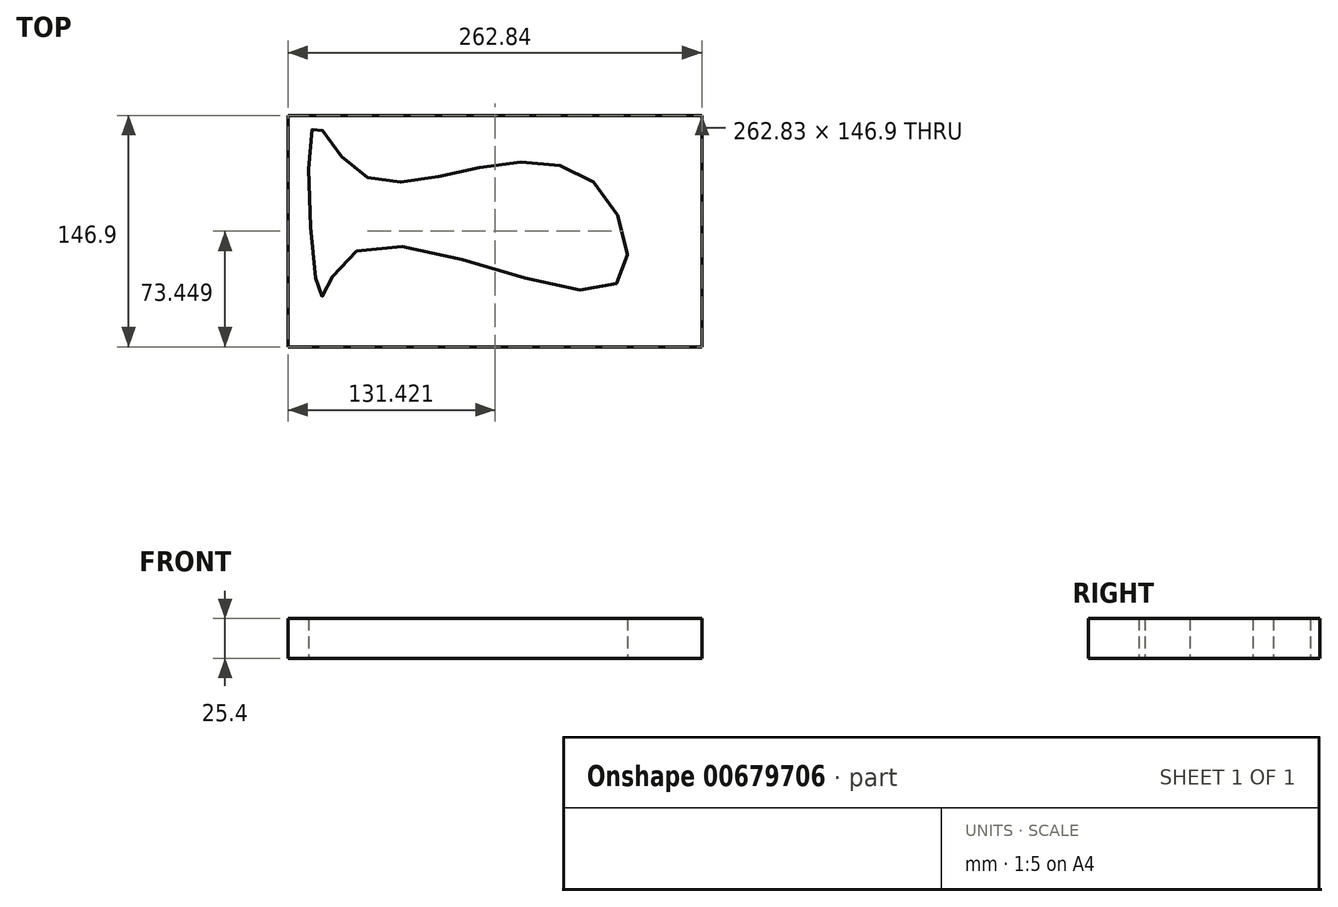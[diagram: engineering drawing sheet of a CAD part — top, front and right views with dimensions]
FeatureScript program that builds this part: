
annotation { "Feature Type Name" : "Feature", "Feature Type Description" : "" }
export const myFeature = defineFeature(function(context is Context, id is Id, definition is map)
    precondition{}
    {
        {
            var Q0;
            Q0=qCreatedBy(makeId("Top.planeOp"),FACE);
            var sketch = newSketch(context, id + "F0", { "sketchPlane" : qUnion([Q0])});
            skLineSegment(sketch, "E0.bottom", {"start": v(-124.76, 81) * mm, "end": v(138.08, 81) * mm});
            skLineSegment(sketch, "E0.top", {"start": v(-124.76, -65.89) * mm, "end": v(138.08, -65.89) * mm});
            skLineSegment(sketch, "E0.left", {"start": v(-124.76, 81) * mm, "end": v(-124.76, -65.89) * mm});
            skLineSegment(sketch, "E0.right", {"start": v(138.08, 81) * mm, "end": v(138.08, -65.89) * mm});
            skSolve(sketch);
        }
        {
            var Q0;
            Q0 = qSketchRegion(id + "F0", true);
            extrude(context, id + "F1", {"entities" : qUnion([Q0]), "depth" : 25.4 * mm, "offsetDistance" : 25.4 * mm});
        }
        {
            var Q0;
            Q0=makeQuery(id+"F1.opExtrude","CAP_FACE",FACE,{"disambiguationData":[OSD([sQuery(id+"F0.wireOp",EDGE,"E0.bottom"),sQuery(id+"F0.wireOp",EDGE,"E0.top"),sQuery(id+"F0.wireOp",EDGE,"E0.left"),sQuery(id+"F0.wireOp",EDGE,"E0.right")])],"isStart":false});
            var sketch = newSketch(context, id + "F2", { "sketchPlane" : qUnion([Q0])});
            skFitSpline(sketch, "E1", {"points": [v(-81.26, -4.94) * mm, v(80.86, -27.62) * mm, v(71.9, 36.22) * mm, v(-10.98, 46.3) * mm, v(-83.22, 46.86) * mm, v(-108.7, 74.02) * mm, v(-104.23, -33.5) * mm, v(-81.26, -4.94) * mm]});
            skSolve(sketch);
        }
        {
            var Q0;
            Q0=makeQuery(id+"F2.imprint","IMPRINT",FACE,{"disambiguationData":[TD([[makeQuery(id+"F2.imprint","IMPRINT",EDGE,{"derivedFrom":sQuery(id+"F2.wireOp",EDGE,"E1")}),1.0]])]});
            extrude(context, id + "F3", {"entities" : qUnion([Q0]), "operationType" : NewBodyOperationType.REMOVE, "endBound" : BoundingType.THROUGH_ALL, "oppositeDirection" : true, "depth" : 25.4 * mm, "hasOffset" : true, "offsetDistance" : 25.4 * mm});
        }
    });
